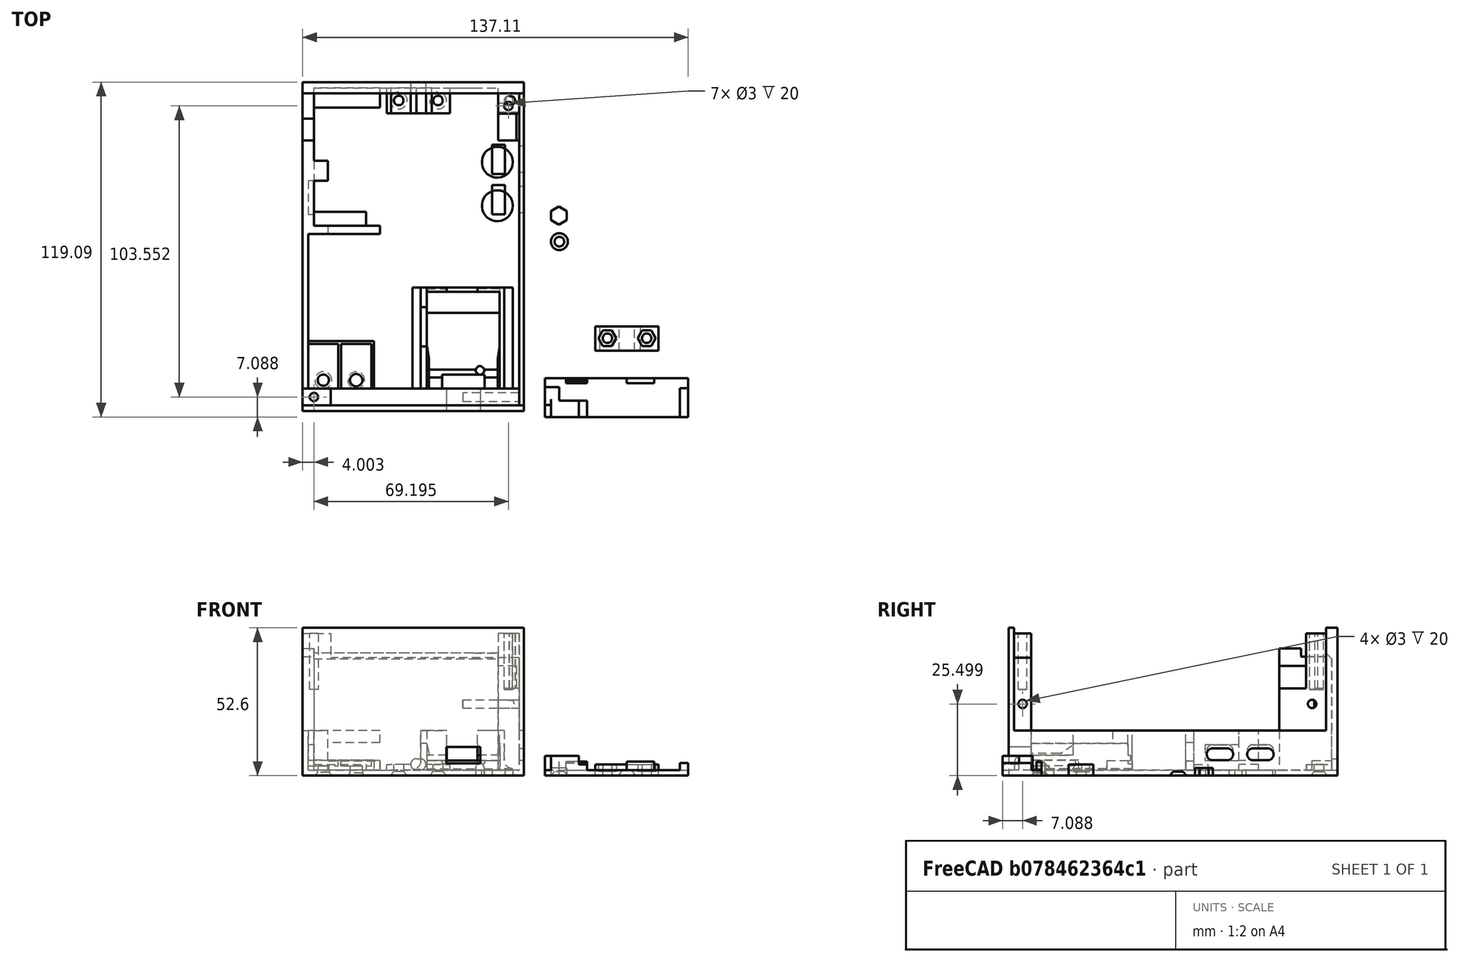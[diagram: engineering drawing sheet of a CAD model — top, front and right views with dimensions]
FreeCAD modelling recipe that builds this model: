
FCSTD DOCUMENT  (FreeCAD 0.18.4R)
Label: control.station.lamp.pump_jack
License: All rights reserved
LicenseURL: http://en.wikipedia.org/wiki/All_rights_reserved
objects: Part::Extrusion×10, Part::Feature×8, Part::Part2DObjectPython×6, Part::Cut×5, Part::MultiFuse×3, Part::Cone×1
note: 33 computed .brp shape members not serialized (recipe doc carries the construction recipe); baked Part::Feature solids carry a one-line shape summary decoded from their .brp

FEATURE [Part::Cut] Cut279012005005031002016006026010003016010
FEATURE [Part::Feature] Cut279012005005031002016006026010003016002  label="Cut279012005005031002016006026010003018"
  Placement = pos=(79.9741,-348.448,-15.9997) rot=(0,0,1;0rad)
  shape: bbox 50.9 x 13.8 x 7 mm, 30 faces (baked)
FEATURE [Part::Cut] Cut002016
  Placement = pos=(9.28133,-91.148,1.02797e-08) rot=(0,0,1;0rad)
FEATURE [Part::Cone] Cone004
  Angle = 360
  AttacherType = Attacher::AttachEngine3D
  Height = 1.5
  Placement = pos=(39.6156,-284.226,-174.501) rot=(0,0,1;0rad)
  Radius1 = 3
  Radius2 = 1.7
FEATURE [Part::Extrusion] Extrusion152050002003013
  Dir = (0,0,-2.7)
  DirMode = 0
  FaceMakerClass = Part::FaceMakerBullseye
  LengthFwd = 0
  LengthRev = 0
  Placement = pos=(-138.772,-49.3483,-2.3) rot=(0,0,1;0.523599rad)
  Solid = true
  Symmetric = false
FEATURE [Part::Feature] Face
  Placement = pos=(-0.233643,0,1.369e-12) rot=(0,0,1;0rad)
  shape: bbox 9.454e-05 x 10.4 x 2 mm, 1 faces, 0 solids (baked)
FEATURE [Part::Extrusion] Extrusion
  Base = -> Face
  Dir = (-4.6,-1e-16,2.69483e-11)
  DirMode = 0
  FaceMakerClass = Part::FaceMakerBullseye
  LengthFwd = 0
  LengthRev = 0
  Solid = true
  Symmetric = false
FEATURE [Part::Feature] Face001
  Placement = pos=(-0.233643,0,1.369e-12) rot=(0,0,1;0rad)
  shape: bbox 9.454e-05 x 10.4 x 2 mm, 1 faces, 0 solids (baked)
FEATURE [Part::Extrusion] Extrusion152050002003014
  Base = -> Face001
  Dir = (-4.6,-1e-16,2.69483e-11)
  DirMode = 0
  FaceMakerClass = Part::FaceMakerBullseye
  LengthFwd = 0
  LengthRev = 0
  Solid = true
  Symmetric = false
FEATURE [Part::Feature] Fusion_solid  label="Fusion (Solid)"
  shape: bbox 78.73 x 117 x 52.6 mm, 313 faces (baked)
FEATURE [Part::Feature] Cut279012005005031002016006026010003016010001  label="Cut279012005005031002016006026010003016011"
  shape: bbox 78.73 x 117 x 52.6 mm, 199 faces (baked)
FEATURE [Part::Part2DObjectPython] Line  # Draft 2D object (typed FeaturePython)
  ChamferSize = 0
  Closed = false
  End = (25.2926,-277.012,-158.501)
  FilletRadius = 0
  Length = 1.73364
  MakeFace = true
  Placement = pos=(27.0263,-277.012,-158.501) rot=(0,0,1;0rad)
  Points = (2) [(0,0,0),(-1.73364,1.70758e-10,-3.17257e-09)]
  Start = (27.0263,-277.012,-158.501)
  Subdivisions = 0
FEATURE [Part::Part2DObjectPython] Rectangle  # Draft 2D object (typed FeaturePython)
  ChamferSize = 0
  Columns = 1
  FilletRadius = 0
  Height = 28.8
  Length = 1.73364
  MakeFace = true
  Placement = pos=(25.2926,-277.012,-158.501) rot=(0,0,1;0rad)
  Rows = 1
FEATURE [Part::Extrusion] Extrusion152050002003015
  Base = -> Rectangle
  Dir = (-1.57567e-09,3.79161e-10,-15.9997)
  DirMode = 0
  FaceMakerClass = Part::FaceMakerBullseye
  LengthFwd = 0
  LengthRev = 0
  Solid = true
  Symmetric = false
FEATURE [Part::MultiFuse] Fusion
  Shapes = -> [Cut279012005005031002016006026010003016010001,Extrusion152050002003015]
FEATURE [Part::Feature] Face002
  Placement = pos=(-0.233643,0,1.369e-12) rot=(0,0,1;0rad)
  shape: bbox 9.454e-05 x 10.4 x 2 mm, 1 faces, 0 solids (baked)
FEATURE [Part::Extrusion] Extrusion152050002003016
  Base = -> Face002
  Dir = (-4.6,-1e-16,2.69483e-11)
  DirMode = 0
  FaceMakerClass = Part::FaceMakerBullseye
  LengthFwd = 0
  LengthRev = 0
  Solid = true
  Symmetric = false
FEATURE [Part::Feature] Face003
  Placement = pos=(-0.233643,0,1.369e-12) rot=(0,0,1;0rad)
  shape: bbox 9.454e-05 x 10.4 x 2 mm, 1 faces, 0 solids (baked)
FEATURE [Part::Extrusion] Extrusion152050002003017
  Base = -> Face003
  Dir = (-4.6,-1e-16,2.69483e-11)
  DirMode = 0
  FaceMakerClass = Part::FaceMakerBullseye
  LengthFwd = 0
  LengthRev = 0
  Solid = true
  Symmetric = false
FEATURE [Part::MultiFuse] Fusion001
  Shapes = -> [Extrusion152050002003016,Extrusion152050002003017,Fusion]
FEATURE [Part::Part2DObjectPython] Circle  # Draft 2D object (typed FeaturePython)
  FirstAngle = 0
  LastAngle = 0
  MakeFace = true
  Placement = pos=(17.5426,-271.442,-172.501) rot=(0,0,1;0rad)
  Radius = 5.5
  Support = -> [Fusion001]
FEATURE [Part::Part2DObjectPython] Circle001  # Draft 2D object (typed FeaturePython)
  FirstAngle = 0
  LastAngle = 0
  MakeFace = true
  Placement = pos=(17.5426,-255.942,-172.501) rot=(0,0,1;0rad)
  Radius = 5.5
  Support = -> [Fusion001]
FEATURE [Part::Extrusion] Extrusion152050002003018
  Base = -> Circle
  Dir = (-7.73061e-09,6.22055e-09,-35.2347)
  DirMode = 0
  FaceMakerClass = Part::FaceMakerBullseye
  LengthFwd = 0
  LengthRev = 0
  Solid = true
  Symmetric = false
FEATURE [Part::Extrusion] Extrusion152050002003019
  Base = -> Circle001
  Dir = (-7.7306e-09,6.22055e-09,-35.2347)
  DirMode = 0
  FaceMakerClass = Part::FaceMakerBullseye
  LengthFwd = 0
  LengthRev = 0
  Solid = true
  Symmetric = false
FEATURE [Part::Cut] Cut
  Base = -> Fusion001
  Tool = -> Extrusion152050002003018
FEATURE [Part::Cut] Cut279012005005031002016006026010003016010002
  Base = -> Cut
  Tool = -> Extrusion152050002003019
FEATURE [Part::Part2DObjectPython] Circle002  # Draft 2D object (typed FeaturePython)
  FirstAngle = 0
  LastAngle = 0
  MakeFace = true
  Placement = pos=(22.1926,-234.012,-123.901) rot=(0,0,1;0rad)
  Radius = 1.7
FEATURE [Part::Extrusion] Extrusion152050002003020
  Base = -> Circle002
  Dir = (-7.28468e-10,-3.79507e-09,-34.6)
  DirMode = 0
  FaceMakerClass = Part::FaceMakerBullseye
  LengthFwd = 0
  LengthRev = 0
  Solid = true
  Symmetric = false
FEATURE [Part::MultiFuse] Fusion002
  Shapes = -> [Cut279012005005031002016006026010003016010002,Extrusion152050002003020]
FEATURE [Part::Part2DObjectPython] Circle003  # Draft 2D object (typed FeaturePython)
  FirstAngle = 0
  LastAngle = 0
  MakeFace = true
  Placement = pos=(21.4881,-235.96,-123.901) rot=(0,0,1;0rad)
  Radius = 1.5
  Support = -> [Fusion002]
FEATURE [Part::Extrusion] Extrusion152050002003021
  Base = -> Circle003
  Dir = (-4.12658e-10,-2.14981e-09,-19.6)
  DirMode = 0
  FaceMakerClass = Part::FaceMakerBullseye
  LengthFwd = 0
  LengthRev = 0
  Solid = true
  Symmetric = false
FEATURE [Part::Cut] Cut279012005005031002016006026010003016010003
  Base = -> Fusion002
  Tool = -> Extrusion152050002003021
FEATURE [Part::Feature] Cut279012005005031002016006026010003016010003001  label="Cut279012005005031002016006026010003016010004"
  shape: bbox 78.73 x 117 x 52.6 mm, 172 faces (baked)
